# Revit family: Tub_Faucet_And_Hand_Shower-Grohe-Plus-23846_Series
name_source: partatom
category: Plumbing Fixtures
revit_build: Autodesk Revit 2018 (Build: 20170223_1515(x64)
units: mm (PartAtom-declared; Revit-internal decimal feet)

## family parameters
Always vertical = No
Cut with Voids When Loaded = No
OmniClass Number = 23.45.05.14.21
OmniClass Title = Bathtubs
Part Type = Normal
Room Calculation Point = No
Round Connector Dimension = Use Diameter
Shared = Yes
Work Plane-Based = Yes

## types (2) — shared parameters
28362000 SilverFlex Shower Hose = Yes
29038001 Rough In Valve = No
ADA Compliant = Yes
Assembly Code = D2020300
CW Connection = No
CWFU = 3
Compliance Certifications = Energy Policy Act of 1992,• NSF 61,• ASME A112.18.1/CSA B125.1
• US Federal and State material regulations,• EPA WaterSense®
Default Elevation = 0"
Description = Plus Single-Handle Freestanding Tub Faucet with 1.75 GPM Hand Shower
Faucet Height = 33 29/32"
Faucet Height Constraint = 33 29/32"
Flow Rate = 1.75 gpm (6.6 l/min)
HW Connection = No
HWFU = 3
Handshower Height = 26 11/16"
Handshower Height Constraint = 26 11/16"
Height = 34 5/8"
Installation Type = Surface Mounted
Length = 11 7/8"
Manufacturer = GROHE
Minimum Operating Pressure = 15 psi (1.0 bar)
Product Documentation Link = https://americanstandard.box.com
Product Page URL = https://www.grohe.us
Tempered Water Connection = Yes
Tempered Water Connection Diameter = 1/2"
URL = https://www.grohe.us
Vent Connection = No
Waste Connection = No
Width = 6 11/16"
cUPC Compliant = Yes
zero-valued in all types: WFU

## per-type parameters (varying)
| type | Finish | Material |
| 23846003 | Metal-Grohe-001-Starlight Chrome | Metal-Grohe-001-Starlight Chrome |
| 23846EN3 | Metal-Grohe-EN3-Brushed Nickel Infinity Finish | Metal-Grohe-EN3-Brushed Nickel Infinity Finish |

note: column(s) folded — value = type name in every type: Model

## geometry (parser evidence)
native form markers: Sweep x5
no freeform markers — native parametric forms only
